# Revit family: Haworth_Planes_ColumnBaseConferenceTable_Key
name_source: partatom
category: Furniture Systems
revit_build: Autodesk Revit 2018 (Build: 20170223_1515(x64)
units: mm (PartAtom-declared; Revit-internal decimal feet)

## family parameters
Always vertical = Yes
Cut with Voids When Loaded = No
OmniClass Number = 23.40.70.14.64.21
OmniClass Title = Systems Furniture
Part Type = Normal
Room Calculation Point = No
Round Connector Dimension = Use Diameter
Shared = No
Work Plane-Based = No

## types (1)
- 84w 60d
    42" Depth Limits = Available Widths = 42, 48, 54, 60 in.
    48" Depth Limits = Available Widths = 48, 54, 60, 66, 72 in.
    54" Depth Limits = Available Widths = 54, 60, 66, 72 in.
    60" Depth Limits = Available Widths = 60, 66, 72, 78, 84 in.
    Actual Depth = 60"
    Actual Height = 41"
    Actual Width = 84"
    Assembly Code = E2020200
    Base Finish = Haworth _ Metal _ Polished Aluminum
    Column Base = Yes
    Column Base Offset = 24 1/2"
    Connect Large Depth = Yes
    Connect Main Finish = Haworth _ Paint _ Metallic Champagne
    Connect Medium Depth = No
    Connect Narrow Width = No
    Connect Switching = Yes
    Connect Trim Finish = Haworth _ Polymer _ Black
    Connect Wide Width = Yes
    Custom Size = No
    Depth = 60"
    Description = Haworth - Planes - Column Base Conference Table - Key
    Height = 41"
    Manufacturer = Haworth
    Max. Depth = 60"
    Max. Height = 41"
    Max. Width = 84"
    Min. Depth = 42"
    Min. Height = 21"
    Min. Width = 60"
    Model = TARY
    Revision Number = 2
    Size = Verify Final Dim. w/ Haworth
    Standard Heights = 21, 29, 41 in.
    Support Finish = Haworth _ Paint _ Metallic Champagne
    Support Height = 39 13/16"
    Sustainability Info = https://www.haworth.com
    Table Thickness = 1 3/16"
    Trim Finish = Haworth _ Paint _ Smoke
    URL = www.haworth.com
    URL - Product = https://www.haworth.com
    Warranty = https://www.haworth.com
    Width = 84"
    Wire Management = Yes
    Wire Management Offset = 5"
    Wire Manager Length = 26"

## geometry (parser evidence)
native form markers: Sweep x14
no freeform markers — native parametric forms only
